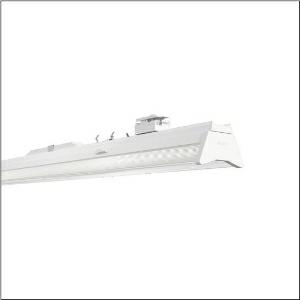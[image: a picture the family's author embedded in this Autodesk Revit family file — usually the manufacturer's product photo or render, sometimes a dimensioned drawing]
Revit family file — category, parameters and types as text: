
# Revit family: licross_r__21_performance_ho_52tm16cn4c5m_51b1
name_source: partatom
category: Lighting Fixtures
units: mm (PartAtom-declared; Revit-internal decimal feet)

## family parameters
Cut with Voids When Loaded = No
Host = Face
Light Source = No
Part Type = Normal
Room Calculation Point = No
Round Connector Dimension = Use Diameter
Shared = No

## types (1)
- --- (1 x LED, 12610 lm, 68.9 W, 4000K)
    Apparent Load = 69 VA
    CIE Flux Codes = 63 87 95 78 100
    Color Rendering = 80
    Color Temperature = 4000K
    Default Elevation = 1800 mm
    Description = Licross® 21 Performance HO, luminaire insert, of sheet steel, galvanised, coil coated, white, length: 1.500mm, width: 120mm, height: 123mm, LED rated luminous flux: 12.610lm, light colour: 840, control gear: ON/OFF Multilumen, CLOi, control gear: ECG Multilumen, with plug, 3-pole, with phase selection, mains connection: 220..240V, AC, 50/60Hz, start of lifetime: 69W, end of service life: 83W, halogen-free wiring, primary light control with lens, of plastic, primary optical cover: cover, of PMMA, light emission: direct/indirect distribution, primary light characteristic: symmetric, protection rating (complete): IP40, insulation class (complete): insulation class I (protective earthing), certification: CE, ENEC, UKCA, protection symbol: D if used in an environment without relevant dust loads with corresponding accessories, impact resistance: IK06, permissible ambient temperature for indoor applications: -35..+35°C, corresponds to IFS (International Featured Standards) requirements for safety and quality in the food industry, reducing of maximum allowable ambient temperature of 5°C with ceiling mounting, LABS conformity tested according to VDMA 24364:2018-05, packaging unit: 1 piece
    Height = 114 mm
    Lamp = 1 x LED
    Lamp Light Flux = 12610 lm
    Lamp Power = 68.9 W
    Lamp count = 1
    Length = 1500 mm
    Luminous efficacy = 183 lm/W
    Manufacturer = Siteco
    ModVariant = No
    Model = 52TM16CN4C5M
    Mounting Place = Ceiling
    Mounting Type = Pendant
    Number of Poles = 1
    OnlyDefault = Yes
    Power Factor = 1
    Product Name = Licross® 21 Performance HO
    Product group = luminaire insert
    ProductGroupID = 902
    Protection Class = Protection class I
    Protection Degree = IP 40
    RLX_Detail_Level = 1
    RLX_Emergency_Light_Flux = 0 lm
    RLX_Emergency_Type = 0
    RLX_Emergency_Type_DB = No
    RlxData = <blob elided: 31805 chars, md5=7f550868>
    Socket = socket
    Standby Power = 0 W
    System Light Flux = 12610 lm
    System Power = 69 W
    Type Comments = factory setting: luminous flux: 100 % | (A | C | E) | 162 mA
    Type Image = l_1256138.jpg
    URL = http://relux.com
    VarID = @adj_111630
    Voltage = 0 V
    Weight = 0.00 kg
    Width = 120 mm

## geometry (parser evidence)
native form markers: Blend x4, Sweep x10
no freeform markers — native parametric forms only
